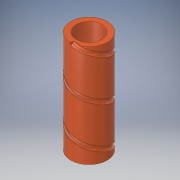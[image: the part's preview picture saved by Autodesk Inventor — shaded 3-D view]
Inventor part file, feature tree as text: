
AUTODESK INVENTOR PART (.ipt)
format: ipt  version: 2019.3 (Build 233278000, 278)  size: 217,600 bytes
history: native  units: in
note: dims shown in document units (in); Inventor stores cm internally (conversion verified against a paired STEP export)
features: sketch x4, extrude x3, helix x1
ambient origin geometry x8: Origin, YZ Plane, XZ Plane, XY Plane, X Axis, Y Axis, Z Axis, Center Point
bodies: Solid1 (feature_tree)
feature tree (8):
  extrude  "Extrusion1"  Depth=5.0in
  helix  "Coil1"  [1 undecoded]
  extrude  "Extrusion6"  TaperAngle=0.0deg  [1 undecoded]
  extrude  "Extrusion5"  Depth=0.125in
  sketch  "Sketch1"  dims[d0=5.0in d1=0.0in d4=1.26in d5=1.78in]
  sketch  "Sketch2"  dims[d10=2.0in d11=1.0in d12=0.9843in d13=0.0in d14=90.0deg d15=90.0deg d16=0.0in d17=0.0in d18=0.25in d23=0.0in]
  sketch  "Sketch10"  dims[d37=0.125in d38=1.25in]
  sketch  "Sketch13"  dims[d40=0.125in d41=2.0in d42=0.0in d48=0.1in d49=0.0309in d50=0.0309in d51=2.0in d52=0.0in]
note: 2 required parameter values undecoded (feature->parameter linkage not recoverable at this tier; creation-order binding heuristic only, values carry confidence <= 0.55)
